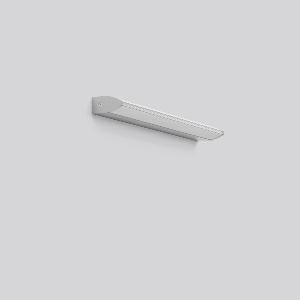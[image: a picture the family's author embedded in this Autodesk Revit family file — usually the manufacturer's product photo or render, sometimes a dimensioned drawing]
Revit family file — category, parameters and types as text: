
# Revit family: lavano_uno_451198_000_b47b
name_source: partatom
category: Lighting Fixtures
units: mm (PartAtom-declared; Revit-internal decimal feet)

## family parameters
Cut with Voids When Loaded = No
Host = Face
Light Source = No
Part Type = Normal
Room Calculation Point = No
Round Connector Dimension = Use Diameter
Shared = No

## types (1)
- LAVANO UNO (1 x LED Modul 830, 1250 lm, 3000)
    Apparent Load = 11 VA
    CIE Flux Codes = 36 62 83 77 100
    Color Rendering = 80
    Color Temperature = 3000
    Default Elevation = 1800 mm
    Description = Series: LAVANO UNO
Linear LED surface-mounted luminaire in an elegant design. Extruded aluminium profile base, lacquered. End caps aluminium, painted. Diffuser: plastic, opal, allows for brilliant glittering light along the lines of the ellipse. Suitable for Ceiling mounting, Wall (surface). 
Colour: white aluminium (RAL 9006)
Length: 580 mm
Width: 40 mm
Height: 83 mm
Lamp: LED
Socket: without socket
Colour temperature: 3000K
Colour rendering index (CRI): 80
System power: 11 W
Rated luminous flux: 1250 lm
Luminous efficiency: 114 lm/W
Control gear: Regulated power supply
Protection class: I
Type of protection: IP 40
    Height = 83 mm
    Lamp = 1 x LED Modul 830
    Lamp Light Flux = 1250 lm
    Lamp count = 1
    Length = 580 mm
    Lifetime = 50000 h
    Luminous efficacy = 114 lm/W
    Manufacturer = RZB
    ModVariant = No
    Model = 451198.000
    Mounting Place = Ceiling, Wall
    Mounting Type = Surface mounted
    Number of Poles = 1
    OnlyDefault = Yes
    Power Factor = 1
    Product Name = LAVANO UNO
    Product group = Surface mounted ceiling and wall luminaires
    ProductGroupID = 305
    Protection Class = Protection class I
    Protection Degree = IP 40
    RLX_Detail_Level = 1
    RLX_Emergency_Light_Flux = 0 lm
    RLX_Emergency_Type = 0
    RLX_Emergency_Type_DB = No
    RlxData = <blob elided: 24753 chars, md5=23856010>
    Socket = socket
    Standby Power = 0 W
    System Light Flux = 1250 lm
    System Power = 11 W
    Type Comments = Product without accessories
    Type Image = 451100.000.jpg
    URL = http://relux.com
    VarID = ---
    Voltage = 230 V
    Voltage Range = 220-240 V
    Weight = 0.00 kg
    Width = 40 mm  [stored 0.131234 ft]

note: [stored X ft] marks values corroborated as IEEE doubles in the binary element streams (Revit-internal decimal feet)

## geometry (parser evidence)
native form markers: Blend x4, Sweep x15
no freeform markers — native parametric forms only
